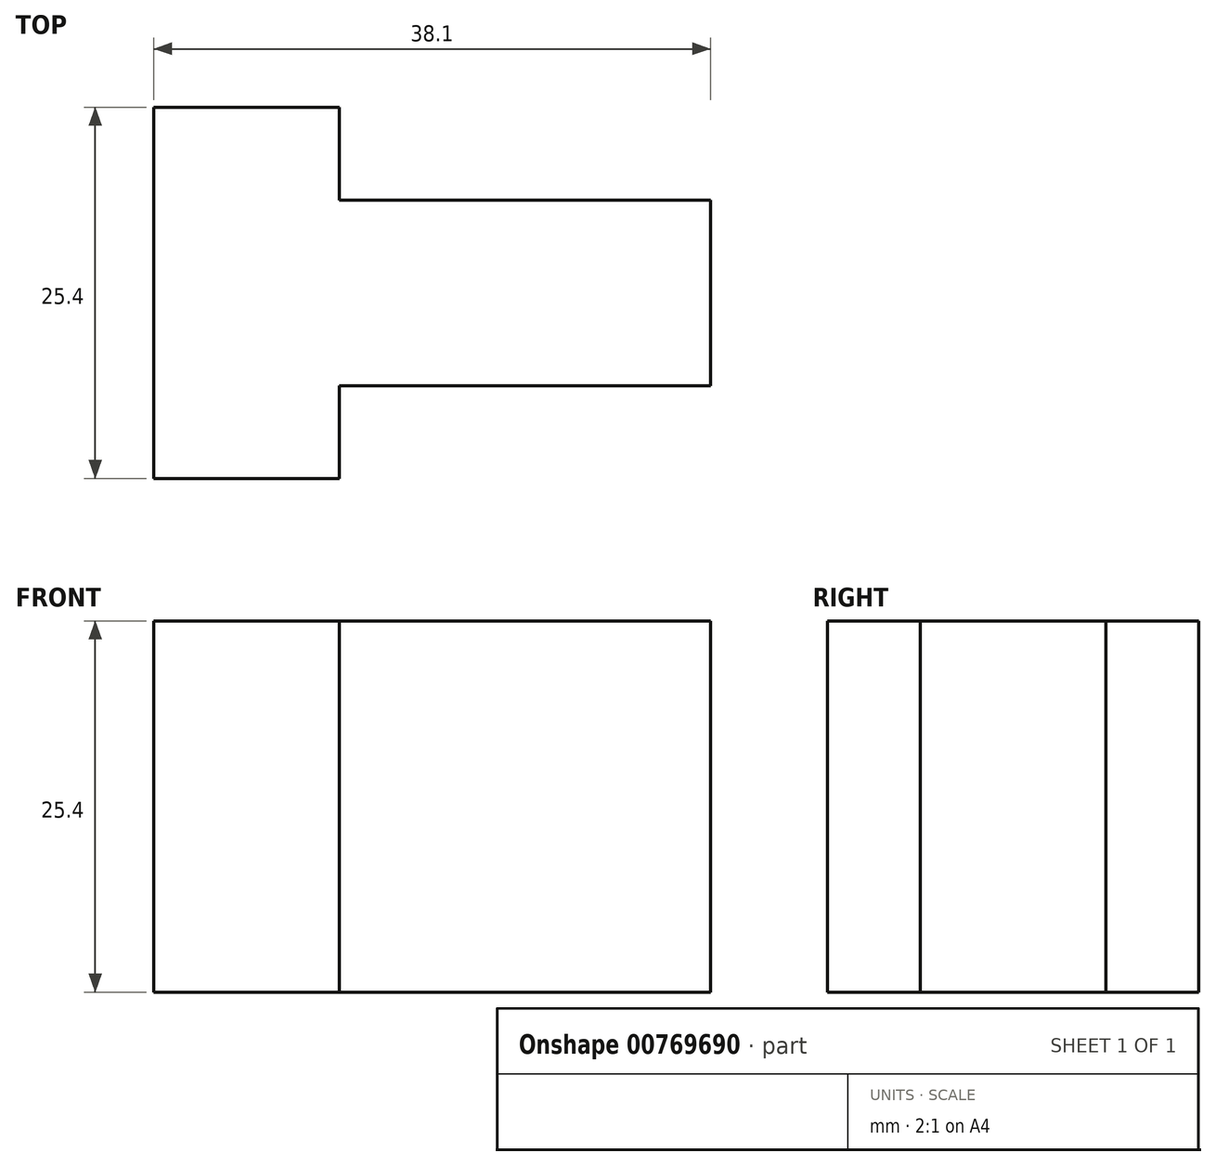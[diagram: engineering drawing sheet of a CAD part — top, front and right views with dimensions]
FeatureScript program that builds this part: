
annotation { "Feature Type Name" : "Feature", "Feature Type Description" : "" }
export const myFeature = defineFeature(function(context is Context, id is Id, definition is map)
    precondition{}
    {
        {
            var Q0;
            Q0=qCreatedBy(makeId("Top.planeOp"),FACE);
            var sketch = newSketch(context, id + "F0", { "sketchPlane" : qUnion([Q0])});
            skLineSegment(sketch, "E0", {"start": v(0, 0) * mm, "end": v(0, 6.35) * mm});
            skLineSegment(sketch, "E1", {"start": v(0, 6.35) * mm, "end": v(25.4, 6.35) * mm});
            skLineSegment(sketch, "E2", {"start": v(25.4, 6.35) * mm, "end": v(25.4, 19.05) * mm});
            skLineSegment(sketch, "E3", {"start": v(25.4, 19.05) * mm, "end": v(0, 19.05) * mm});
            skLineSegment(sketch, "E4", {"start": v(0, 19.05) * mm, "end": v(0, 25.4) * mm});
            skLineSegment(sketch, "E5", {"start": v(0, 25.4) * mm, "end": v(-12.7, 25.4) * mm});
            skLineSegment(sketch, "E6", {"start": v(-12.7, 25.4) * mm, "end": v(-12.7, 0) * mm});
            skLineSegment(sketch, "E7", {"start": v(-12.7, 0) * mm, "end": v(0, 0) * mm});
            skSolve(sketch);
        }
        {
            var Q0;
            Q0 = qSketchRegion(id + "F0", true);
            extrude(context, id + "F1", {"entities" : qUnion([Q0]), "depth" : 25.4 * mm, "offsetDistance" : 25.4 * mm});
        }
    });
